# Revit family: HL_Корпус плоского душевого лотка InFloor_HL541Q
name_source: partatom
category: Plumbing Fixtures
revit_build: Autodesk Revit 2016 (Build: 20161004_0715(x64)
units: mm (PartAtom-declared; Revit-internal decimal feet)

## family parameters
Always vertical = Yes
Cut with Voids When Loaded = No
OmniClass Number = 23.70.50.21.24.14
OmniClass Title = Deck Waste Water Drains
Part Type = Normal
Room Calculation Point = Yes
Round Connector Dimension = Use Diameter
Shared = No
Work Plane-Based = No

## types (1)
- HL_Корпус плоского душевого лотка InFloor_HL541Q
    CW Connection = No
    Description = Душевой трап
    EAN = 9003076048236
    HW Connection = No
    Keynote = HL541Q
    Manufacturer = HL Hutterer & Lechner GmbH
    Model = HL541Q
    Type Comments = Душевой трап «PRIMUS-BLUE» с монтажными уголками, дизайн-решёткой из нержавеющей стали «Quadra», гидроизоляционным комплектом
    URL = http://www.hutterer-lechner.com
    Vent Connection = No
    Waste Connection = Yes
    ВЕС = 1,39 kg
    ВЫСОТА МОНТАЖА = 62-200mm (Estrichoberkante)
    МАКСИМАЛЬНАЯ НАГРУЗКА КЛАССА = K3 - 300kg
    МАТЕРИАЛ = PP/Edelstahl
    НАСАДКА = Edelstahl V4A 10-30mm/121x121
    ПРОИЗВОДИТЕЛЬНОСТЬ = 0,44l/s
    РАЗМЕР = DN40/50
    РЕШЁТКА = Edelstahl V4A 115x115/62x62

## geometry (parser evidence)
native form markers: Sweep x5
no freeform markers — native parametric forms only
